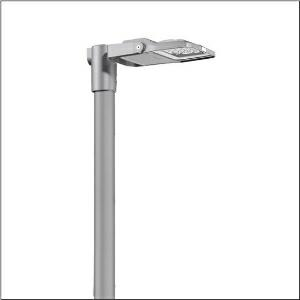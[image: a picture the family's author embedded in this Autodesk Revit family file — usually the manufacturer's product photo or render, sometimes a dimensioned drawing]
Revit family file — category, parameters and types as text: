
# Revit family: floodlight_fl_21_iq_micro___pl33t_5xa7762a4f3a_b73c
name_source: partatom
category: Lighting Fixtures
units: mm (PartAtom-declared; Revit-internal decimal feet)

## family parameters
Cut with Voids When Loaded = No
Host = Face
Light Source = No
Part Type = Normal
Room Calculation Point = No
Round Connector Dimension = Use Diameter
Shared = No

## types (1)
- --- (1 x LED, 3050 lm, 23.1 W, 4000K)
    Apparent Load = 23 VA
    CIE Flux Codes = 26 75 99 100 100
    Color Rendering = 70
    Color Temperature = 4000K
    Default Elevation = 1800 mm
    Description = Floodlight FL 21 iQ micro, floodlight, primary light control with lens, of PMMA, primary optical cover: protective disc, of toughened safety glass, transparent, light distribution: PL33T, light emission: direct distribution, installation type: surface-mounted, lamps: LED, High Power LED, rated values: 3.050lm | 23,1W | 132lm/W (begin service life); end service life: 3.050lm | 23,8W; at 50% lumin. flux: 1.525lm | 11W | 138,6lm/W, colour temperature: 4000K, colour rendering: CRI > 70, light colour: 740, light setting 1 begin service life: 100% | 3.050lm | 23,1W | 132lm/W | 4.000K, light setting 1 end service life: 23,8W, further light settings possible, control: Auto-Match, Temp-Guard, Night-Set, Smart-Wire, Desk-Remote (wireless, voltage-free reading and setting of iQ features in the workshop via application-optimized NFC function/RFID function), optimised constant luminous flux control (CLO 2.0), Street-Remote, pre-setting: linear dimming characteristic, with terminal, 6-pole, mains connection: 220..240V, AC, 50/60Hz, luminaire housing, of diecast aluminium, powder-coated, SITECO metallic grey (DB 702S), corrosivity category C5 mid according to DIN EN ISO 12944suitable for swimming poolschlorine-resistant, sealing non-destructively replaceable, please order mast flange separately, mast bracket, of steel, galvanised, powder-coated, SITECO metallic grey (DB 702S), protection rating (complete): IP66, insulation class (complete): insulation class II (safety insulation), certification: CE, ENEC, VDE, protection symbol: D, impact resistance: IK07, permissible operating ambient temperature: -40..+40°C, permissible operating ambient temperature for outdoor applications: -40..+50°C, standard: DIN EN 12944, LABS conformity tested according to VDMA 24364:2018-05, packaging unit: 1 piece

Light Distribution: PL33T
    Height = 65 mm
    Lamp = 1 x LED
    Lamp Light Flux = 3050 lm
    Lamp Power = 23.1 W
    Lamp count = 1
    Length = 312 mm
    Luminous efficacy = 132 lm/W
    Manufacturer = Siteco
    ModVariant = No
    Model = 5XA7762A4F3A
    Number of Poles = 1
    OnlyDefault = Yes
    Power Factor = 1
    Product Name = Floodlight FL 21 iQ micro | PL33T
    Product group = floodlight | pylon annexe
    ProductGroupID = 6201
    Protection Class = Protection class II
    Protection Degree = IP 66
    RLX_Detail_Level = 1
    RLX_Emergency_Light_Flux = 0 lm
    RLX_Emergency_Type = 0
    RLX_Emergency_Type_DB = No
    RlxData = <blob elided: 101929 chars, md5=1a84d785>
    Socket = socket
    Standby Power = 0 W
    System Light Flux = 3050 lm
    System Power = 23 W
    Type Comments = factory setting: luminous flux: 100 % | dim-lin: 254 | 455 mA
    Type Image = l_1007121.jpg
    URL = http://relux.com
    VarID = @adj_147353
    Voltage = 0 V
    Weight = 0.00 kg
    Width = 230 mm

## geometry (parser evidence)
native form markers: Blend x4, Sweep x11
no freeform markers — native parametric forms only
